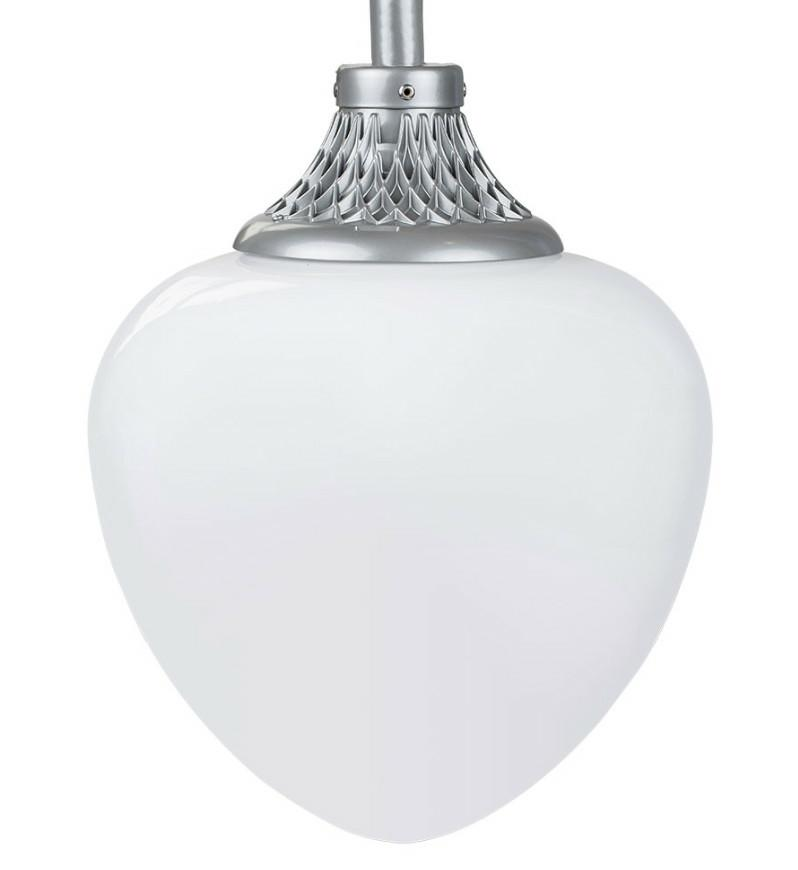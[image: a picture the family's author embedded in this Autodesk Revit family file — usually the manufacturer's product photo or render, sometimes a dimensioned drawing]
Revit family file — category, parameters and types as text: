
# Revit family: GALAD Капля LED
name_source: partatom
category: Осветительные приборы
revit_build: Autodesk Revit 2018 (Build: 20180423_1000(x64)
units: mm (PartAtom-declared; Revit-internal decimal feet)

## family parameters
Источник света = Да
Общий = Нет
Основа = Грань
При загрузке вырезать с полостями = Нет
Размер круглого соединителя = Использовать диаметр
Тип детали = Нормальный
Точка расчета площади = Нет

## types (1)
- GALAD Капля LED
    ADSK_Версия Revit = 2018
    ADSK_Версия семейства = 1.01
    ADSK_Единица измерения = шт.
    ADSK_Завод-изготовитель = Лихославльский завод 'Светотехника'
    ADSK_Классификация нагрузок = Освещение
    ADSK_Код изделия = 13843
    ADSK_Количество = 1
    ADSK_Количество фаз = 1
    ADSK_Коэффициент мощности = 0.96
    ADSK_Марка = GALAD Капля LED-40-СПШ/С1 (3700/750/RAL7040/D/0/GEN1)
    ADSK_Масса = 4.2
    ADSK_Масса_Текст = 4.2
    ADSK_Наименование = GALAD Капля LED-40-СПШ/С1 (3700/750/RAL7040/D/0/GEN1)
    ADSK_Наименование краткое = GALAD Капля LED-40-СПШ/С1
    ADSK_Напряжение = 230 В
    ADSK_Номинальная мощность = 40 В·А
    ADSK_Обозначение = ГОСТ Р 54350, ГОСТ 12.2.007.0, 
ГОСТ 17516.1, ГОСТ 15150
    ADSK_Полная мощность = 42 В·А
    ADSK_Размер_Высота = 537 мм
    ADSK_Размер_Длина = 400 мм
    ADSK_Размер_Ширина = 400 мм
    ADSK_Ток = 0 А
    ADSK_Энергоэффективность = 93 лм/Вт
    IP = 65
    URL = https://galad.ru
    Блок аварийного питания = Нет
    Возможный угол наклона = 0
    Группа модели = Светильники
    Диапазон цветовой температуры = 5028±283
    Изготовитель = Лихославльский завод 'Светотехника'
    Класс Защиты = 1
    Класс защиты от поражения электрическим током = 1
    Класс светораспределения = Р
    Климатическая зона = У1
    Климатическое исполнение = -40…40 °С
    Коэффициент пульсации = менее 10%
    Материал корпуса = Литой алюминий
    Материал рассеивателя = Ударопрочный поликарбонат
    Неравномерность яркости = 0
    Область использования = Садово-парковое освещение
    Описание = Классическая, привычная всем, форма светильника в современном светодиодном исполнении. Такие светильники освещают парки, скверы, бульвары, а иногда даже и улицы каждого российского города. Цельнолитое основание обеспечивает оптимальный теплоотвод, а антивандальный рассеиватель из ударопрочного светостабилизированного поликарбоната лучше сохраняет свой внешний вид и оптические свойства, по сравнению с обычным поликарбонатом.
    Отметка по умолчанию = 1219 мм
    Полная установленная мощность = 42 В·А
    Световая отдача = 93
    Светофильтр = 16777215
    Смещение цветовой температуры при затухании лампы = <Нет>
    Снижение светового потока во время разгорания = не более 6%
    Срок службы = 12 лет
    Тип КСС = специальная полуширокая
    Тип ПРА = ЭПРА
    Тип источника света = LED
    Тип монтажной поверхности = торшер
    Тип продукции = Светильник
    Тип устройства управления светодиодами = без управления
    Угол наклона = -90.00°
    Файл фотометрической сетки = GALAD Kaplya LED.IES
    Цветопередача = 80
    Частота = 50
